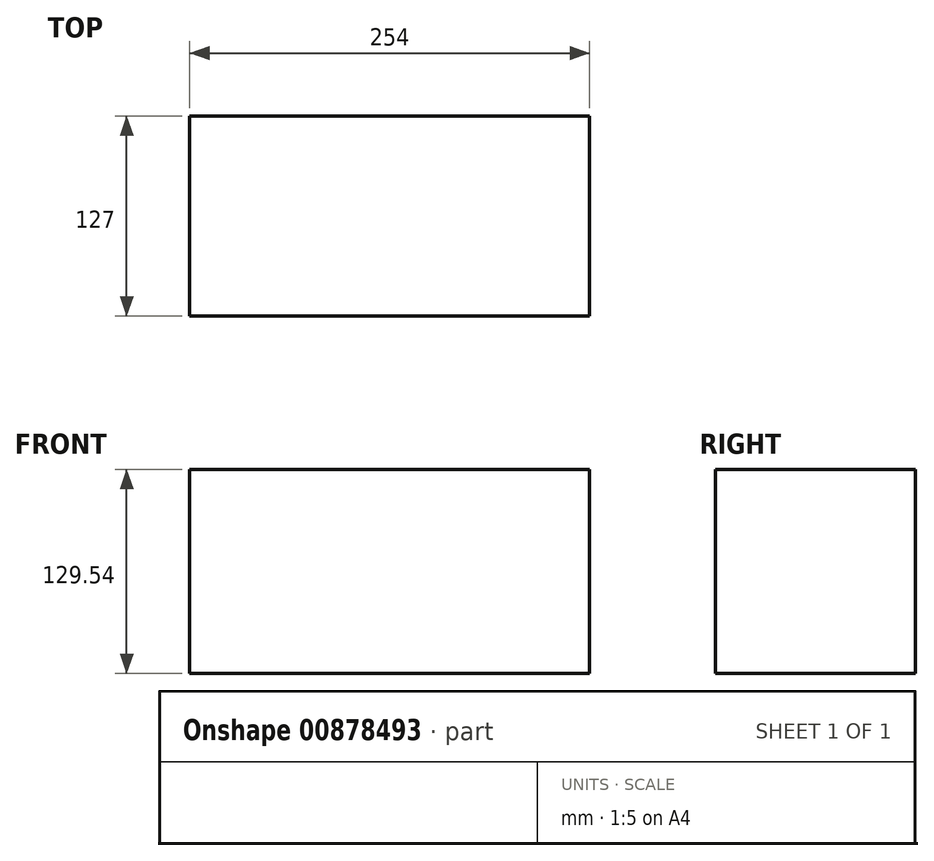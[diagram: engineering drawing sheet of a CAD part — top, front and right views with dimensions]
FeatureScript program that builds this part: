
annotation { "Feature Type Name" : "Feature", "Feature Type Description" : "" }
export const myFeature = defineFeature(function(context is Context, id is Id, definition is map)
    precondition{}
    {
        {
            var Q0;
            Q0=qCreatedBy(makeId("Top.planeOp"),FACE);
            var sketch = newSketch(context, id + "F0", { "sketchPlane" : qUnion([Q0])});
            skLineSegment(sketch, "E0.bottom", {"start": v(-38.87, 63.5) * mm, "end": v(-292.87, 63.5) * mm});
            skLineSegment(sketch, "E0.top", {"start": v(-38.87, -63.5) * mm, "end": v(-292.87, -63.5) * mm});
            skLineSegment(sketch, "E0.left", {"start": v(-38.87, 63.5) * mm, "end": v(-38.87, -63.5) * mm});
            skLineSegment(sketch, "E0.right", {"start": v(-292.87, 63.5) * mm, "end": v(-292.87, -63.5) * mm});
            skPoint(sketch, "E0.middle", {"position": v(-165.87, 0) * mm});
            skSolve(sketch);
        }
        {
            var Q0;
            Q0=makeQuery(id+"F0.imprint","IMPRINT",FACE,{"disambiguationData":[TD([[makeQuery(id+"F0.imprint","IMPRINT",EDGE,{"derivedFrom":sQuery(id+"F0.wireOp",EDGE,"E0.bottom")}),1.0]])]});
            extrude(context, id + "F1", {"entities" : qUnion([Q0]), "depth" : 129.54 * mm, "offsetDistance" : 25.4 * mm});
        }
    });
